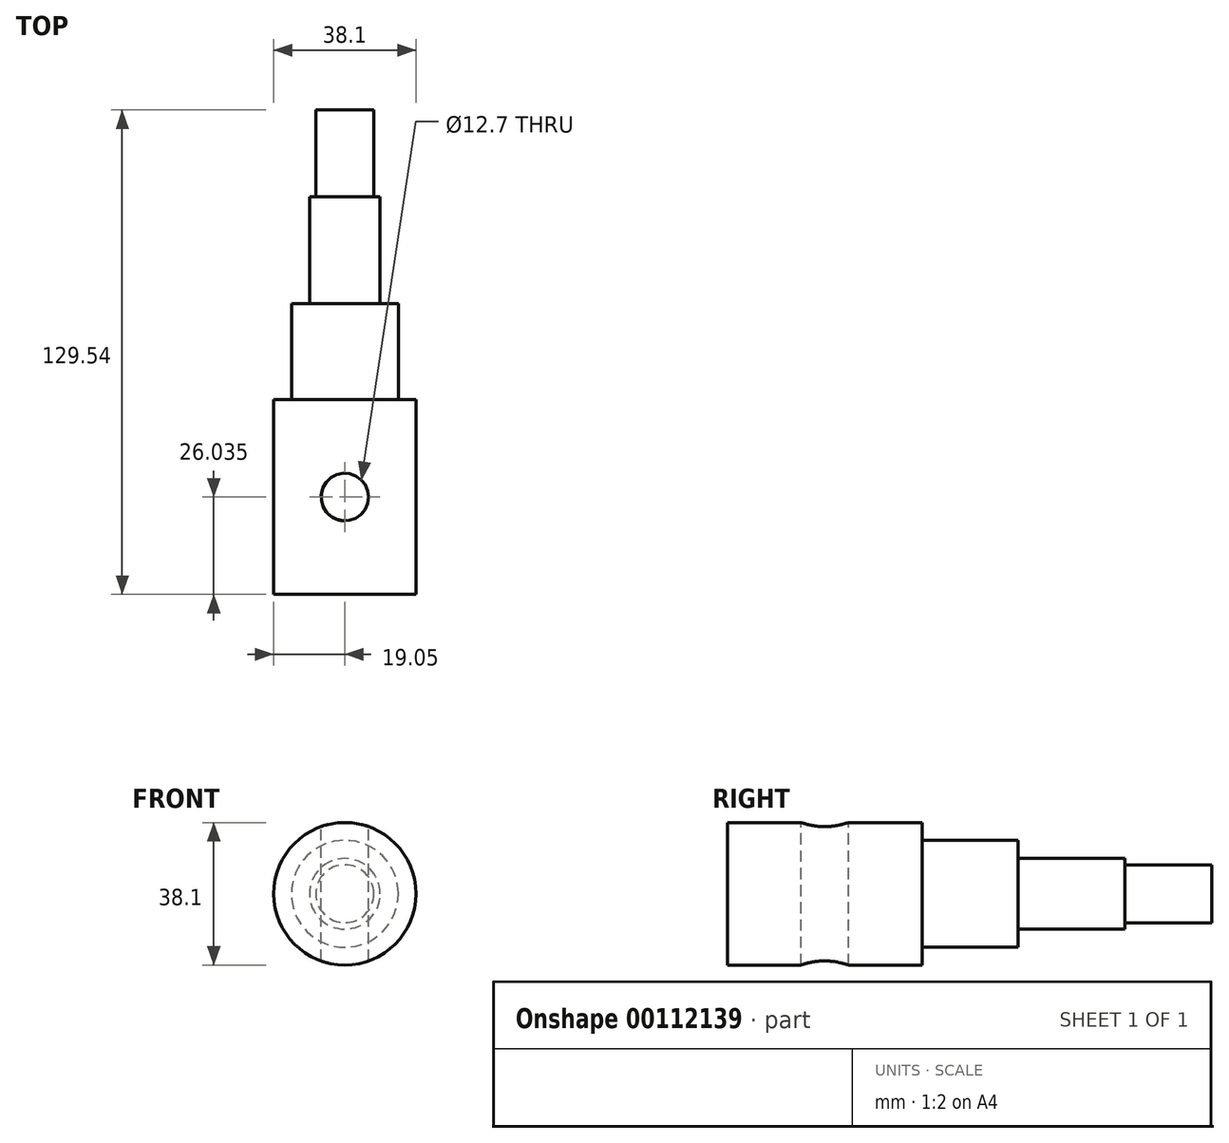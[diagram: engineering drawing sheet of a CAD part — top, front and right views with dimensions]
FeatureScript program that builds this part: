
annotation { "Feature Type Name" : "Feature", "Feature Type Description" : "" }
export const myFeature = defineFeature(function(context is Context, id is Id, definition is map)
    precondition{}
    {
        {
            var Q0;
            Q0=qCreatedBy(makeId("Right.planeOp"),FACE);
            var sketch = newSketch(context, id + "F0", { "sketchPlane" : qUnion([Q0])});
            skLineSegment(sketch, "E0.bottom", {"start": v(0, 19.05) * mm, "end": v(52.07, 19.05) * mm});
            skLineSegment(sketch, "E0.top", {"start": v(0, 0) * mm, "end": v(52.07, 0) * mm});
            skLineSegment(sketch, "E0.left", {"start": v(0, 19.05) * mm, "end": v(0, 0) * mm});
            skLineSegment(sketch, "E0.right", {"start": v(52.07, 19.05) * mm, "end": v(52.07, 0) * mm});
            skLineSegment(sketch, "E1.bottom", {"start": v(52.07, 14.29) * mm, "end": v(77.72, 14.29) * mm});
            skLineSegment(sketch, "E1.top", {"start": v(52.07, 0) * mm, "end": v(77.72, 0) * mm});
            skLineSegment(sketch, "E1.left", {"start": v(52.07, 14.29) * mm, "end": v(52.07, 0) * mm});
            skLineSegment(sketch, "E1.right", {"start": v(77.72, 14.29) * mm, "end": v(77.72, 0) * mm});
            skLineSegment(sketch, "E2.bottom", {"start": v(77.72, 9.45) * mm, "end": v(106.3, 9.45) * mm});
            skLineSegment(sketch, "E2.top", {"start": v(77.72, 0) * mm, "end": v(106.3, 0) * mm});
            skLineSegment(sketch, "E2.left", {"start": v(77.72, 9.45) * mm, "end": v(77.72, 0) * mm});
            skLineSegment(sketch, "E2.right", {"start": v(106.3, 9.45) * mm, "end": v(106.3, 0) * mm});
            skLineSegment(sketch, "E3.bottom", {"start": v(106.3, 7.75) * mm, "end": v(129.54, 7.75) * mm});
            skLineSegment(sketch, "E3.top", {"start": v(106.3, 0) * mm, "end": v(129.54, 0) * mm});
            skLineSegment(sketch, "E3.left", {"start": v(106.3, 7.75) * mm, "end": v(106.3, 0) * mm});
            skLineSegment(sketch, "E3.right", {"start": v(129.54, 7.75) * mm, "end": v(129.54, 0) * mm});
            skSolve(sketch);
        }
        {
            var Q0;
            Q0 = qSketchRegion(id + "F0", true);
            var Q1;
            Q1=sQuery(id+"F0.wireOp",EDGE,"E0.top");
            revolve(context, id + "F1", {"entities" : qUnion([Q0]), "axis" : qUnion([Q1]), "revolveType" : RevolveType.FULL});
        }
        {
            var Q0;
            Q0=qCreatedBy(makeId("Top.planeOp"),FACE);
            var sketch = newSketch(context, id + "F2", { "sketchPlane" : qUnion([Q0])});
            skCircle(sketch, "E4", {"center": v(0, 26.04) * mm, "radius": 6.35 * mm});
            skSolve(sketch);
        }
        {
            var Q0;
            Q0 = qSketchRegion(id + "F2", true);
            extrude(context, id + "F3", {"entities" : qUnion([Q0]), "operationType" : NewBodyOperationType.REMOVE, "endBound" : BoundingType.THROUGH_ALL, "oppositeDirection" : true, "depth" : 25.4 * mm, "hasSecondDirection" : true, "secondDirectionBound" : SecondDirectionBoundingType.THROUGH_ALL, "secondDirectionOppositeDirection" : false, "secondDirectionDepth" : 25.4 * mm});
        }
    });
